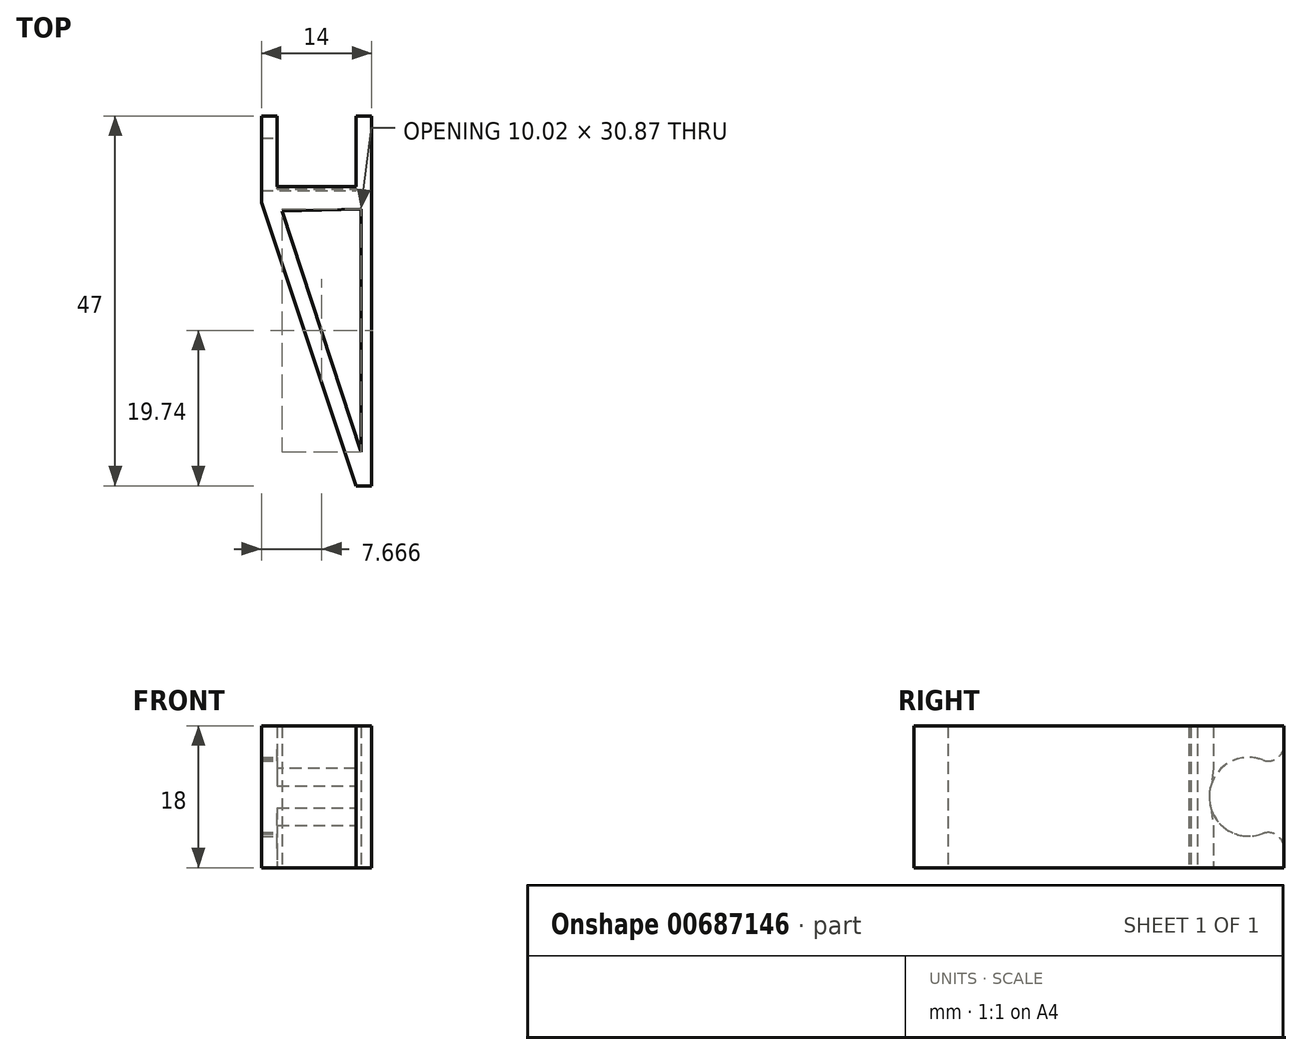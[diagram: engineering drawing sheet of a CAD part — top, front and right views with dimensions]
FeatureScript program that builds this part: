
annotation { "Feature Type Name" : "Feature", "Feature Type Description" : "" }
export const myFeature = defineFeature(function(context is Context, id is Id, definition is map)
    precondition{}
    {
        {
            var Q0;
            Q0=qCreatedBy(makeId("Top.planeOp"),FACE);
            var sketch = newSketch(context, id + "F0", { "sketchPlane" : qUnion([Q0])});
            skLineSegment(sketch, "E0", {"start": v(0, 23.67) * mm, "end": v(0, -23.33) * mm});
            skLineSegment(sketch, "E1", {"start": v(0, -23.33) * mm, "end": v(-2, -23.33) * mm});
            skLineSegment(sketch, "E2", {"start": v(-14, 12.67) * mm, "end": v(-14, 23.67) * mm});
            skLineSegment(sketch, "E3", {"start": v(-14, 23.67) * mm, "end": v(-12, 23.67) * mm});
            skLineSegment(sketch, "E4", {"start": v(-12, 23.67) * mm, "end": v(-12, 14.7) * mm});
            skLineSegment(sketch, "E5", {"start": v(-12, 14.7) * mm, "end": v(-2, 14.7) * mm});
            skLineSegment(sketch, "E6", {"start": v(-2, 14.7) * mm, "end": v(-2, 23.67) * mm});
            skLineSegment(sketch, "E7", {"start": v(-2, 23.67) * mm, "end": v(0, 23.67) * mm});
            skLineSegment(sketch, "E8", {"start": v(-14, 12.67) * mm, "end": v(-2, -23.33) * mm});
            skSolve(sketch);
        }
        {
            var Q0;
            Q0=qSketchRegion(id+"F0",true);
            extrude(context, id + "F1", {"entities" : qUnion([Q0]), "depth" : 18 * mm, "offsetDistance" : 25 * mm});
        }
        {
            var Q0;
            Q0=makeQuery(id+"F1.opExtrude","SWEPT_FACE",FACE,{"disambiguationData":[OSD([sQuery(id+"F0.wireOp",EDGE,"E4")])]});
            var sketch = newSketch(context, id + "F2", { "sketchPlane" : qUnion([Q0])});
            skCircle(sketch, "E9", {"center": v(19.18, 9) * mm, "radius": 5 * mm});
            skPoint(sketch, "E9.centerSnap0", {"position": v(23.67, 9) * mm});
            skPoint(sketch, "E9.centerSnap1", {"position": v(19.18, 0) * mm});
            skSolve(sketch);
        }
        {
            var Q0;
            Q0=qSketchRegion(id+"F2",true);
            extrude(context, id + "F3", {"entities" : qUnion([Q0]), "operationType" : NewBodyOperationType.REMOVE, "oppositeDirection" : true, "depth" : 5 * mm, "offsetDistance" : 25 * mm});
        }
        {
            var Q0;
            Q0=makeQuery(id+"F3.boolean.opBoolean","INTERSECT",EDGE,{"disambiguationData":[OD(1.0)],"derivedFrom":[makeQuery(id+"F1.opExtrude","SWEPT_FACE",FACE,{"disambiguationData":[OSD([sQuery(id+"F0.wireOp",EDGE,"E3")])]}),makeQuery(id+"F3.opExtrude","SWEPT_FACE",FACE,{"disambiguationData":[OSD([sQuery(id+"F2.wireOp",EDGE,"E9")])]})]});
            var Q1;
            Q1=makeQuery(id+"F3.boolean.opBoolean","INTERSECT",EDGE,{"disambiguationData":[OD(0.0)],"derivedFrom":[makeQuery(id+"F1.opExtrude","SWEPT_FACE",FACE,{"disambiguationData":[OSD([sQuery(id+"F0.wireOp",EDGE,"E3")])]}),makeQuery(id+"F3.opExtrude","SWEPT_FACE",FACE,{"disambiguationData":[OSD([sQuery(id+"F2.wireOp",EDGE,"E9")])]})]});
            chamfer(context, id + "F4", {"entities" : qUnion([Q0, Q1]), "chamferType" : ChamferType.TWO_OFFSETS, "width1" : 5 * mm, "oppositeDirection" : false, "width2" : 4 * mm, "tangentPropagation" : true});
        }
        {
            var Q0;
            Q0=qSketchRegion(id+"F2",true);
            extrude(context, id + "F5", {"entities" : qUnion([Q0]), "operationType" : NewBodyOperationType.REMOVE, "depth" : 10 * mm, "offsetDistance" : 25 * mm});
        }
        {
            var Q0;
            Q0=makeQuery(id+"F5.boolean.opBoolean","INTERSECT",EDGE,{"disambiguationData":[OD(0.0)],"derivedFrom":[makeQuery(id+"F1.opExtrude","SWEPT_FACE",FACE,{"disambiguationData":[OSD([sQuery(id+"F0.wireOp",EDGE,"E5")])]}),makeQuery(id+"F5.opExtrude","SWEPT_FACE",FACE,{"disambiguationData":[OSD([sQuery(id+"F2.wireOp",EDGE,"E9")])]})]});
            var Q1;
            Q1=makeQuery(id+"F5.boolean.opBoolean","INTERSECT",EDGE,{"disambiguationData":[OD(1.0)],"derivedFrom":[makeQuery(id+"F1.opExtrude","SWEPT_FACE",FACE,{"disambiguationData":[OSD([sQuery(id+"F0.wireOp",EDGE,"E5")])]}),makeQuery(id+"F5.opExtrude","SWEPT_FACE",FACE,{"disambiguationData":[OSD([sQuery(id+"F2.wireOp",EDGE,"E9")])]})]});
            chamfer(context, id + "F6", {"entities" : qUnion([Q0, Q1]), "width" : 8 * mm, "tangentPropagation" : true});
        }
        {
            var Q0;
            {var subQ0=sQuery(id+"F0.wireOp",EDGE,"E4");var subQ1=sQuery(id+"F0.wireOp",EDGE,"E3");var subQ2=sQuery(id+"F0.wireOp",EDGE,"E2");var subQ3=makeQuery(id+"F3.opExtrude","SWEPT_FACE",FACE,{"disambiguationData":[OSD([sQuery(id+"F2.wireOp",EDGE,"E9")])]});var subQ4=makeQuery(id+"F1.opExtrude","SWEPT_FACE",FACE,{"disambiguationData":[OSD([subQ1])]});Q0=makeQuery(id+"F4.opChamfer","BLEND_EDGE",EDGE,{"blendedFrom":[makeQuery(id+"F3.boolean.opBoolean","INTERSECT",EDGE,{"disambiguationData":[OD(1.0)],"derivedFrom":[subQ4,subQ3]}),makeQuery(id+"F3.boolean.opBoolean","SPLIT",FACE,{"disambiguationData":[TD([makeQuery(id+"F1.opExtrude","CAP_FACE",FACE,{"disambiguationData":[OSD([sQuery(id+"F0.wireOp",EDGE,"E0"),sQuery(id+"F0.wireOp",EDGE,"E1"),subQ2,subQ1,subQ0,sQuery(id+"F0.wireOp",EDGE,"E5"),sQuery(id+"F0.wireOp",EDGE,"E6"),sQuery(id+"F0.wireOp",EDGE,"E7"),sQuery(id+"F0.wireOp",EDGE,"E8")])],"isStart":false})])],"derivedFrom":subQ4})],"blendedInto":[makeQuery(id+"F3.boolean.opBoolean","SPLIT",FACE,{"disambiguationData":[TD([makeQuery(id+"F1.opExtrude","CAP_FACE",FACE,{"disambiguationData":[OSD([sQuery(id+"F0.wireOp",EDGE,"E0"),sQuery(id+"F0.wireOp",EDGE,"E1"),subQ2,subQ1,subQ0,sQuery(id+"F0.wireOp",EDGE,"E5"),sQuery(id+"F0.wireOp",EDGE,"E6"),sQuery(id+"F0.wireOp",EDGE,"E7"),sQuery(id+"F0.wireOp",EDGE,"E8")])],"isStart":false})])],"derivedFrom":subQ4})]});}
            var Q1;
            {var subQ0=sQuery(id+"F0.wireOp",EDGE,"E4");var subQ1=sQuery(id+"F0.wireOp",EDGE,"E3");var subQ2=sQuery(id+"F0.wireOp",EDGE,"E2");var subQ3=makeQuery(id+"F3.opExtrude","SWEPT_FACE",FACE,{"disambiguationData":[OSD([sQuery(id+"F2.wireOp",EDGE,"E9")])]});var subQ4=makeQuery(id+"F1.opExtrude","SWEPT_FACE",FACE,{"disambiguationData":[OSD([subQ1])]});Q1=makeQuery(id+"F4.opChamfer","BLEND_EDGE",EDGE,{"blendedFrom":[makeQuery(id+"F3.boolean.opBoolean","INTERSECT",EDGE,{"disambiguationData":[OD(0.0)],"derivedFrom":[subQ4,subQ3]}),makeQuery(id+"F3.boolean.opBoolean","SPLIT",FACE,{"disambiguationData":[TD([makeQuery(id+"F1.opExtrude","CAP_FACE",FACE,{"disambiguationData":[OSD([sQuery(id+"F0.wireOp",EDGE,"E0"),sQuery(id+"F0.wireOp",EDGE,"E1"),subQ2,subQ1,subQ0,sQuery(id+"F0.wireOp",EDGE,"E5"),sQuery(id+"F0.wireOp",EDGE,"E6"),sQuery(id+"F0.wireOp",EDGE,"E7"),sQuery(id+"F0.wireOp",EDGE,"E8")])],"isStart":true})])],"derivedFrom":subQ4})],"blendedInto":[makeQuery(id+"F3.boolean.opBoolean","SPLIT",FACE,{"disambiguationData":[TD([makeQuery(id+"F1.opExtrude","CAP_FACE",FACE,{"disambiguationData":[OSD([sQuery(id+"F0.wireOp",EDGE,"E0"),sQuery(id+"F0.wireOp",EDGE,"E1"),subQ2,subQ1,subQ0,sQuery(id+"F0.wireOp",EDGE,"E5"),sQuery(id+"F0.wireOp",EDGE,"E6"),sQuery(id+"F0.wireOp",EDGE,"E7"),sQuery(id+"F0.wireOp",EDGE,"E8")])],"isStart":true})])],"derivedFrom":subQ4})]});}
            fillet(context, id + "F7", {"entities" : qUnion([Q0, Q1]), "radius" : 2 * mm, "tangentPropagation" : true, "allowEdgeOverflow" : false});
        }
        {
            var Q0;
            Q0=qCreatedBy(makeId("Top.planeOp"),FACE);
            var sketch = newSketch(context, id + "F8", { "sketchPlane" : qUnion([Q0])});
            skLineSegment(sketch, "E10", {"start": v(-1.32, 11.84) * mm, "end": v(-1.32, -19.02) * mm});
            skLineSegment(sketch, "E11", {"start": v(-1.32, -19.02) * mm, "end": v(-11.35, 11.58) * mm});
            skLineSegment(sketch, "E12", {"start": v(-11.35, 11.58) * mm, "end": v(-1.32, 11.84) * mm});
            skSolve(sketch);
        }
        {
            var Q0;
            Q0 = qSketchRegion(id + "F8", true);
            extrude(context, id + "F9", {"entities" : qUnion([Q0]), "operationType" : NewBodyOperationType.REMOVE, "depth" : 28.4 * mm, "offsetDistance" : 25 * mm});
        }
    });
